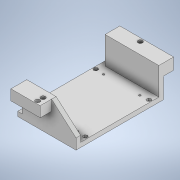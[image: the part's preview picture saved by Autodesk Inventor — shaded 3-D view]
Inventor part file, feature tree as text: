
AUTODESK INVENTOR PART (.ipt)
format: ipt  version: 2020 (Build 240168000, 168)  size: 302,592 bytes
history: native  units: mm
features: sketch x7, projected_geometry x6, extrude x5, other x4, hole x2, mirror x1
ambient origin geometry x8: Origin, YZ Plane, XZ Plane, XY Plane, X Axis, Y Axis, Z Axis, Center Point
bodies: Body1 (feature_tree)
feature tree (25):
  other  "tray4_L.ipt"
  mirror  "미러1"
  extrude  "돌출1"  Depth=10.0mm
  extrude  "돌출2"  Depth=10.0mm TaperAngle=0.0deg
  extrude  "돌출3"  Depth=10.0mm TaperAngle=0.0deg
  hole  "구멍1"  [1 undecoded]
  hole  "구멍2"  [1 undecoded]
  extrude  "돌출4"  Depth=140.0mm
  extrude  "돌출5"  Depth=80.0mm
  other  "솔리드1::tray4_L.ipt"
  other  "피쳐 태그1"
  sketch  "스케치1"
  projected_geometry  "투영된 루프1"
  sketch  "스케치2"
  sketch  "스케치3"
  projected_geometry  "투영된 루프2"
  sketch  "스케치5"
  projected_geometry  "투영된 루프3"
  sketch  "스케치6"
  projected_geometry  "투영된 루프4"
  sketch  "스케치7"
  projected_geometry  "투영된 루프5"
  sketch  "스케치8"
  projected_geometry  "투영된 루프6"
  other  "솔리드1"
note: 2 required parameter values undecoded (feature->parameter linkage not recoverable at this tier; creation-order binding heuristic only, values carry confidence <= 0.55)
